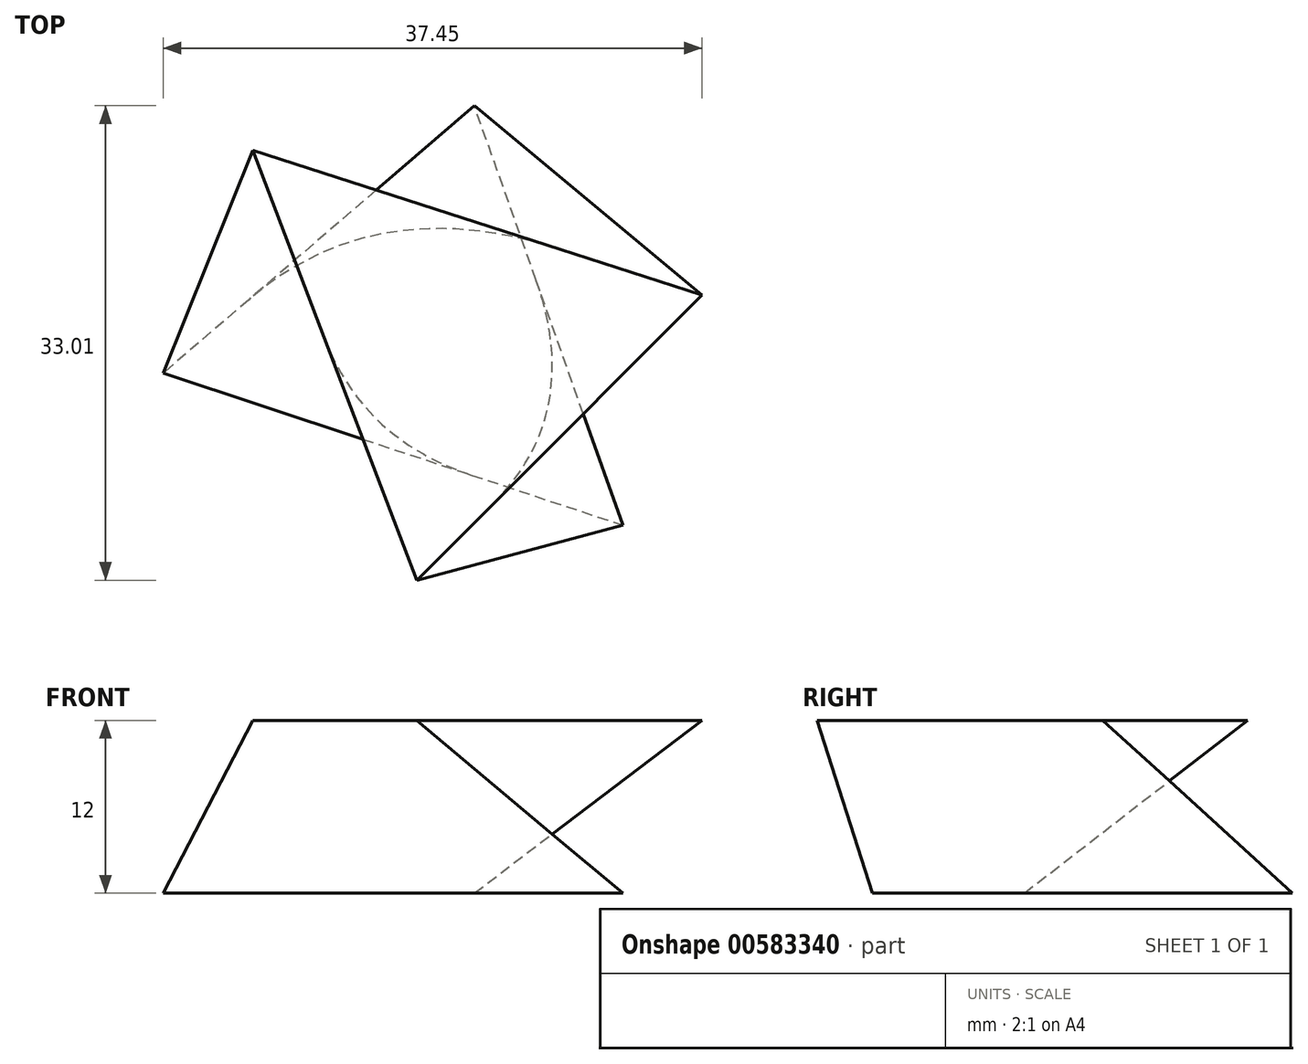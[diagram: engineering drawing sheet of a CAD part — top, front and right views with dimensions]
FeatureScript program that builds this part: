
annotation { "Feature Type Name" : "Feature", "Feature Type Description" : "" }
export const myFeature = defineFeature(function(context is Context, id is Id, definition is map)
    precondition{}
    {
        {
            var Q0;
            Q0=qCreatedBy(makeId("Top.planeOp"),FACE);
            cPlane(context, id + "F0", {"entities" : qUnion([Q0]), "cplaneType" : CPlaneType.OFFSET, "offset" : 2 * mm, "oppositeDirection" : true, "width" : 150 * mm, "height" : 150 * mm});
        }
        {
            var Q0;
            Q0=qCreatedBy(id+"F0.planeOp",FACE);
            cPlane(context, id + "F1", {"entities" : qUnion([Q0]), "cplaneType" : CPlaneType.OFFSET, "offset" : 15 * mm, "oppositeDirection" : true, "width" : 150 * mm, "height" : 150 * mm});
        }
        {
            var Q0;
            Q0=qCreatedBy(id+"F0.planeOp",FACE);
            var sketch = newSketch(context, id + "F2", { "sketchPlane" : qUnion([Q0])});
            skLineSegment(sketch, "E0", {"start": v(23.4, 1.78) * mm, "end": v(-1.4, -23.03) * mm});
            skLineSegment(sketch, "E1", {"start": v(-1.4, -23.03) * mm, "end": v(-15.62, 14.33) * mm});
            skLineSegment(sketch, "E2", {"start": v(-15.62, 14.33) * mm, "end": v(23.4, 1.78) * mm});
            skSolve(sketch);
        }
        {
            var Q0;
            Q0=qCreatedBy(id+"F1.planeOp",FACE);
            var sketch = newSketch(context, id + "F3", { "sketchPlane" : qUnion([Q0])});
            skLineSegment(sketch, "E3", {"start": v(3.61, 18.23) * mm, "end": v(-23.42, -5.03) * mm});
            skLineSegment(sketch, "E4", {"start": v(-23.42, -5.03) * mm, "end": v(16.5, -18.23) * mm});
            skLineSegment(sketch, "E5", {"start": v(16.5, -18.23) * mm, "end": v(3.61, 18.23) * mm});
            skSolve(sketch);
        }
        {
            var Q1;
            Q1=makeQuery(id+"F3.imprint","IMPRINT",FACE,{"disambiguationData":[TD([[makeQuery(id+"F3.imprint","IMPRINT",EDGE,{"derivedFrom":sQuery(id+"F3.wireOp",EDGE,"E3")}),1.0]])]});
            var Q2;
            Q2=makeQuery(id+"F2.imprint","IMPRINT",FACE,{"disambiguationData":[TD([[makeQuery(id+"F2.imprint","IMPRINT",EDGE,{"derivedFrom":sQuery(id+"F2.wireOp",EDGE,"E0")}),-1.0]])]});
            loft(context, id + "F4", {"sheetProfilesArray" : [{ "sheetProfileEntities" : qUnion([Q1]) }, { "sheetProfileEntities" : qUnion([Q2]) }]});
        }
        {
            var Q0;
            Q0=makeQuery(id+"F4.opLoft","SWEPT_BODY",BODY,{"disambiguationData":[OSD([makeQuery(id+"F2.imprint","IMPRINT",FACE,{"disambiguationData":[TD([[makeQuery(id+"F2.imprint","IMPRINT",EDGE,{"derivedFrom":sQuery(id+"F2.wireOp",EDGE,"E0")}),-1.0]])]}),makeQuery(id+"F3.imprint","IMPRINT",FACE,{"disambiguationData":[TD([[makeQuery(id+"F3.imprint","IMPRINT",EDGE,{"derivedFrom":sQuery(id+"F3.wireOp",EDGE,"E3")}),1.0]])]})])]});
            var Q1;
            Q1=makeQuery(id+"F4.opLoft","MID_CAP_VERTEX",VERTEX,{"disambiguationData":[OSD([sQuery(id+"F3.wireOp",EDGE,"E3"),sQuery(id+"F3.wireOp",EDGE,"E4")])],"capPos":0.0});
            transform(context, id + "F5", {"entities" : qUnion([Q0]), "transformType" : TransformType.SCALE_UNIFORMLY, "scale" : .8, "scalePoint" : qUnion([Q1]), "makeCopy" : false});
        }
    });
